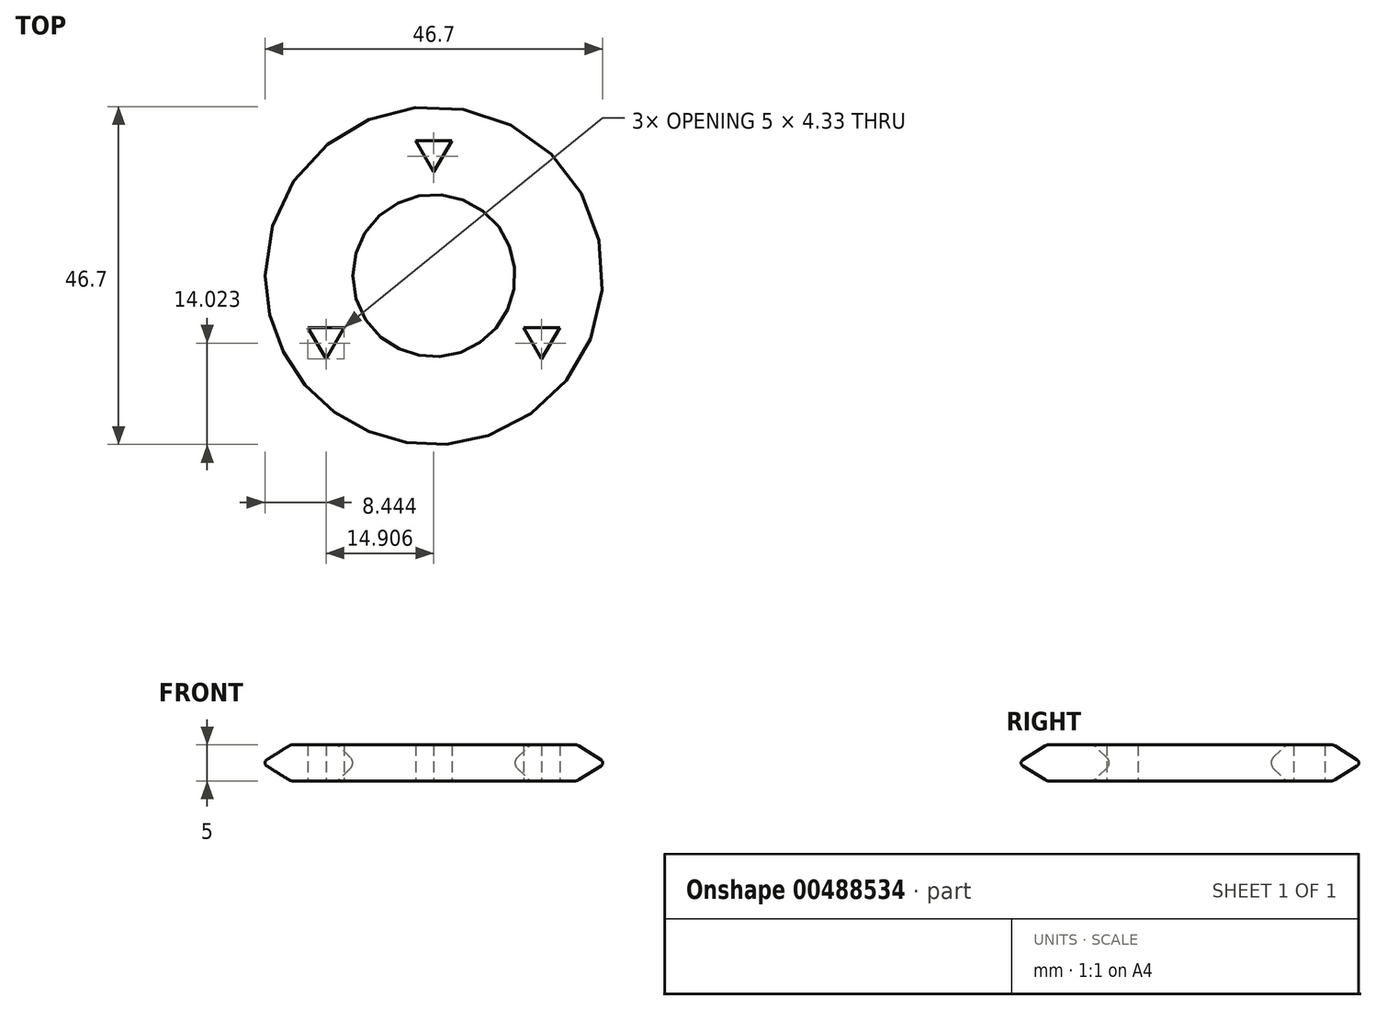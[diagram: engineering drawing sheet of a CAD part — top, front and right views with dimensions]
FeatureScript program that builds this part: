
annotation { "Feature Type Name" : "Feature", "Feature Type Description" : "" }
export const myFeature = defineFeature(function(context is Context, id is Id, definition is map)
    precondition{}
    {
        {
            var Q0;
            Q0=qCreatedBy(makeId("Front.planeOp"),FACE);
            var sketch = newSketch(context, id + "F0", { "sketchPlane" : qUnion([Q0])});
            skLineSegment(sketch, "E0.bottom", {"start": v(-19.5, 5) * mm, "end": v(-13.73, 5) * mm});
            skLineSegment(sketch, "E0.top", {"start": v(-19.5, 0) * mm, "end": v(-13.73, 0) * mm});
            skLineSegment(sketch, "E1", {"start": v(-20.04, 4.85) * mm, "end": v(-23.12, 2.92) * mm});
            skLineSegment(sketch, "E2", {"start": v(-23.12, 2.08) * mm, "end": v(-20.04, 0.15) * mm});
            skPoint(sketch, "E3.visualSharp", {"position": v(-19.8, 5) * mm});
            skArc(sketch, "E3.filletArc", {"start": v(-19.5, 5) * mm, "mid": v(-19.78, 4.96) * mm, "end": v(-20.04, 4.85) * mm});
            skPoint(sketch, "E4.visualSharp", {"position": v(-19.8, 0) * mm});
            skArc(sketch, "E4.filletArc", {"start": v(-20.04, 0.15) * mm, "mid": v(-19.78, 0.04) * mm, "end": v(-19.5, 0) * mm});
            skPoint(sketch, "E5.visualSharp", {"position": v(-23.8, 2.5) * mm});
            skArc(sketch, "E5.filletArc", {"start": v(-23.12, 2.92) * mm, "mid": v(-23.35, 2.5) * mm, "end": v(-23.12, 2.08) * mm});
            skLineSegment(sketch, "E6", {"start": v(-13.02, 4.7) * mm, "end": v(-11.51, 3.2) * mm});
            skLineSegment(sketch, "E7", {"start": v(-11.51, 1.8) * mm, "end": v(-13.02, 0.3) * mm});
            skPoint(sketch, "E0.right.end.orphan", {"position": v(0, 0) * mm});
            skPoint(sketch, "E8.visualSharp", {"position": v(-10.8, 2.5) * mm});
            skArc(sketch, "E8.filletArc", {"start": v(-11.51, 1.8) * mm, "mid": v(-11.22, 2.5) * mm, "end": v(-11.51, 3.2) * mm});
            skPoint(sketch, "E9.visualSharp", {"position": v(-13.31, 5) * mm});
            skArc(sketch, "E9.filletArc", {"start": v(-13.02, 4.7) * mm, "mid": v(-13.35, 4.92) * mm, "end": v(-13.73, 5) * mm});
            skPoint(sketch, "E10.visualSharp", {"position": v(-13.31, 0) * mm});
            skArc(sketch, "E10.filletArc", {"start": v(-13.73, 0) * mm, "mid": v(-13.35, 0.08) * mm, "end": v(-13.02, 0.3) * mm});
            skSolve(sketch);
        }
        {
            var Q0;
            Q0=qCreatedBy(makeId("Front.planeOp"),FACE);
            var sketch = newSketch(context, id + "F1", { "sketchPlane" : qUnion([Q0])});
            skLineSegment(sketch, "E11", {"start": v(0, 0) * mm, "end": v(0, 73.49) * mm});
            skSolve(sketch);
        }
        {
            var Q0;
            Q0 = qSketchRegion(id + "F0", true);
            var Q1;
            Q1=sQuery(id+"F1.wireOp",EDGE,"E11");
            revolve(context, id + "F2", {"entities" : qUnion([Q0]), "axis" : qUnion([Q1]), "revolveType" : RevolveType.FULL});
        }
        {
            var Q0;
            Q0=qCreatedBy(makeId("Top.planeOp"),FACE);
            var sketch = newSketch(context, id + "F3", { "sketchPlane" : qUnion([Q0])});
            skLineSegment(sketch, "E12.0", {"start": v(-2.5, 18.65) * mm, "end": v(2.5, 18.65) * mm});
            skLineSegment(sketch, "E12.1", {"start": v(2.5, 18.65) * mm, "end": v(0, 14.32) * mm});
            skLineSegment(sketch, "E12.2", {"start": v(0, 14.32) * mm, "end": v(-2.5, 18.65) * mm});
            skPoint(sketch, "E12.0.midPoint", {"position": v(0, 18.65) * mm});
            skLineSegment(sketch, "E13.1.0", {"start": v(-17.4, -7.16) * mm, "end": v(-12.4, -7.16) * mm});
            skLineSegment(sketch, "E13.1.2", {"start": v(-14.9, -11.5) * mm, "end": v(-17.4, -7.16) * mm});
            skLineSegment(sketch, "E13.1.3", {"start": v(-12.4, -7.16) * mm, "end": v(-14.9, -11.5) * mm});
            skLineSegment(sketch, "E13.2.0", {"start": v(14.9, -11.5) * mm, "end": v(12.4, -7.16) * mm});
            skLineSegment(sketch, "E13.2.2", {"start": v(17.4, -7.16) * mm, "end": v(14.9, -11.5) * mm});
            skLineSegment(sketch, "E13.2.3", {"start": v(12.4, -7.16) * mm, "end": v(17.4, -7.16) * mm});
            skPoint(sketch, "E13.center", {"position": v(0, 0) * mm});
            skSolve(sketch);
        }
        {
            var Q0;
            Q0=makeQuery(id+"F3.imprint","IMPRINT",FACE,{"disambiguationData":[TD([[makeQuery(id+"F3.imprint","IMPRINT",EDGE,{"derivedFrom":sQuery(id+"F3.wireOp",EDGE,"E12.0")}),-1.0]])]});
            var Q1;
            Q1=makeQuery(id+"F3.imprint","IMPRINT",FACE,{"disambiguationData":[TD([[makeQuery(id+"F3.imprint","IMPRINT",EDGE,{"derivedFrom":sQuery(id+"F3.wireOp",EDGE,"E13.1.0")}),-1.0]])]});
            var Q2;
            Q2=makeQuery(id+"F3.imprint","IMPRINT",FACE,{"disambiguationData":[TD([[makeQuery(id+"F3.imprint","IMPRINT",EDGE,{"derivedFrom":sQuery(id+"F3.wireOp",EDGE,"E13.2.0")}),-1.0]])]});
            extrude(context, id + "F4", {"entities" : qUnion([Q0, Q1, Q2]), "operationType" : NewBodyOperationType.REMOVE, "depth" : 25 * mm, "offsetDistance" : 25 * mm});
        }
    });
